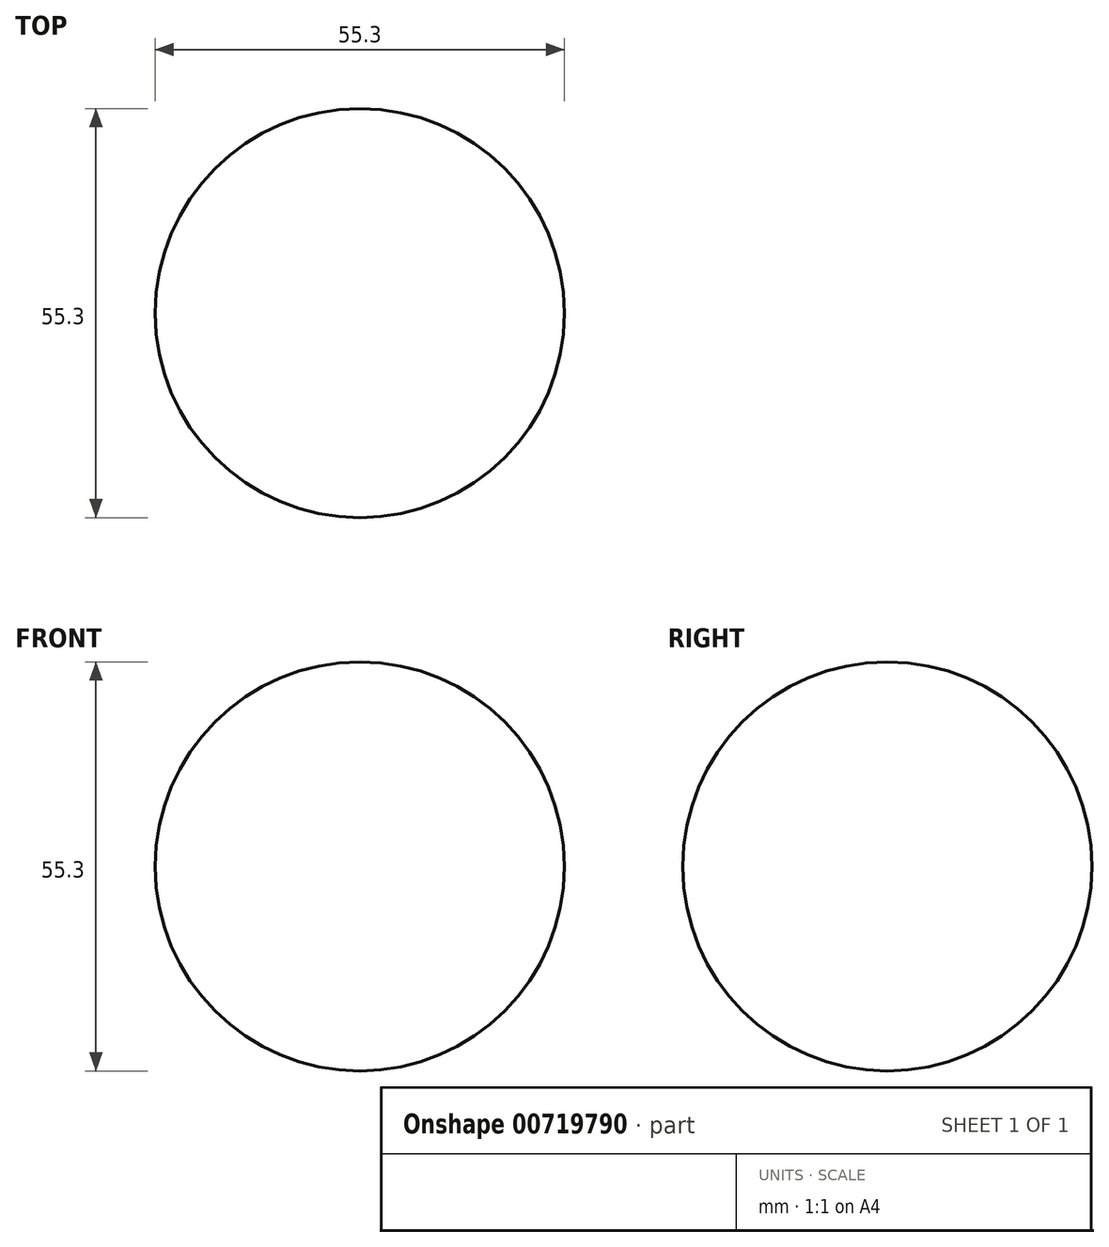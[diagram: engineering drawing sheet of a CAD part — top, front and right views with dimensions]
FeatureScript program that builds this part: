
annotation { "Feature Type Name" : "Feature", "Feature Type Description" : "" }
export const myFeature = defineFeature(function(context is Context, id is Id, definition is map)
    precondition{}
    {
        {
            var Q0;
            Q0=qCreatedBy(makeId("Front.planeOp"),FACE);
            var sketch = newSketch(context, id + "F0", { "sketchPlane" : qUnion([Q0])});
            skArc(sketch, "E0", {"start": v(27.65, 0) * mm, "mid": v(0, 27.65) * mm, "end": v(-27.65, 0) * mm});
            skSolve(sketch);
        }
        {
            var Q0;
            Q0=qCreatedBy(makeId("Front.planeOp"),FACE);
            var sketch = newSketch(context, id + "F1", { "sketchPlane" : qUnion([Q0])});
            skLineSegment(sketch, "E1", {"start": v(-27.65, 0) * mm, "end": v(27.65, 0) * mm});
            skSolve(sketch);
        }
        {
            var Q0;
            Q0=sQuery(id+"F0.wireOp",EDGE,"E0");
            var Q1;
            Q1=sQuery(id+"F1.wireOp",EDGE,"E1");
            revolve(context, id + "F2", {"bodyType" : ToolBodyType.SURFACE, "surfaceOperationType" : NewSurfaceOperationType.NEW, "surfaceEntities" : qUnion([Q0]), "axis" : qUnion([Q1]), "revolveType" : RevolveType.FULL});
        }
    });
